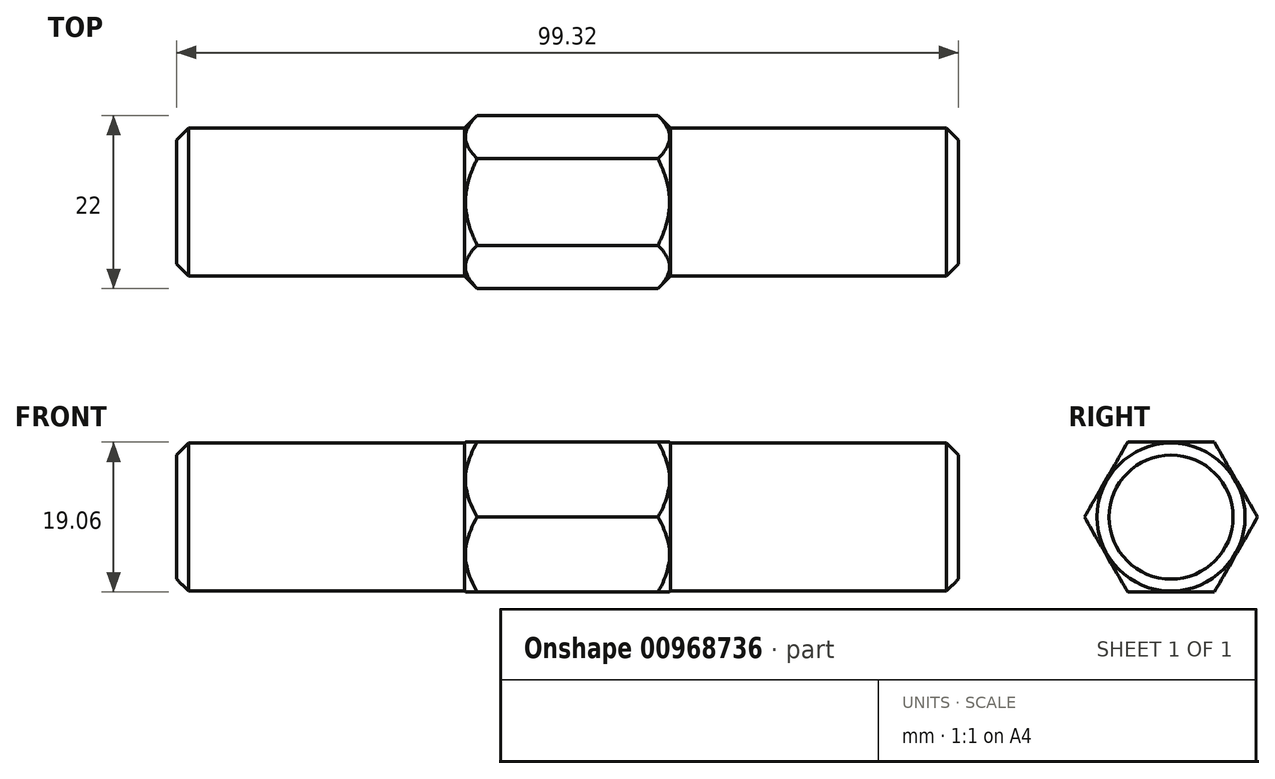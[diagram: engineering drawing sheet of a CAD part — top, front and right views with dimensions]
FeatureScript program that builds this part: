
annotation { "Feature Type Name" : "Feature", "Feature Type Description" : "" }
export const myFeature = defineFeature(function(context is Context, id is Id, definition is map)
    precondition{}
    {
        {
            var Q0;
            Q0=qCreatedBy(makeId("Right.planeOp"),FACE);
            var sketch = newSketch(context, id + "F0", { "sketchPlane" : qUnion([Q0])});
            skCircle(sketch, "E0.cCircle", {"center": v(0, 0) * mm, "radius": 9.53 * mm, "construction": true});
            skLineSegment(sketch, "E0.0", {"start": v(11, 0) * mm, "end": v(5.5, -9.53) * mm});
            skLineSegment(sketch, "E0.1", {"start": v(5.5, -9.53) * mm, "end": v(-5.5, -9.53) * mm});
            skLineSegment(sketch, "E0.2", {"start": v(-5.5, -9.52) * mm, "end": v(-11, 0) * mm});
            skLineSegment(sketch, "E0.3", {"start": v(-11, 0) * mm, "end": v(-5.5, 9.52) * mm});
            skLineSegment(sketch, "E0.4", {"start": v(-5.5, 9.52) * mm, "end": v(5.5, 9.52) * mm});
            skLineSegment(sketch, "E0.5", {"start": v(5.5, 9.52) * mm, "end": v(11, 0) * mm});
            skPoint(sketch, "E0.0.midPoint", {"position": v(8.25, -4.76) * mm});
            skSolve(sketch);
        }
        {
            var Q0;
            Q0=makeQuery(id+"F0.imprint","IMPRINT",FACE,{"disambiguationData":[TD([[makeQuery(id+"F0.imprint","IMPRINT",EDGE,{"derivedFrom":sQuery(id+"F0.wireOp",EDGE,"E0.0")}),-1.0]])]});
            extrude(context, id + "F1", {"entities" : qUnion([Q0]), "depth" : 13.08 * mm, "offsetDistance" : 25.4 * mm});
        }
        {
            var Q0;
            Q0=makeQuery(id+"F1.opExtrude","CAP_FACE",FACE,{"disambiguationData":[OSD([sQuery(id+"F0.wireOp",EDGE,"E0.0"),sQuery(id+"F0.wireOp",EDGE,"E0.1"),sQuery(id+"F0.wireOp",EDGE,"E0.2"),sQuery(id+"F0.wireOp",EDGE,"E0.3"),sQuery(id+"F0.wireOp",EDGE,"E0.4"),sQuery(id+"F0.wireOp",EDGE,"E0.5")])],"isStart":false});
            var sketch = newSketch(context, id + "F2", { "sketchPlane" : qUnion([Q0])});
            skCircle(sketch, "E1", {"center": v(0, 0) * mm, "radius": 9.4 * mm});
            skSolve(sketch);
        }
        {
            var Q0;
            Q0=makeQuery(id+"F2.imprint","IMPRINT",FACE,{"disambiguationData":[TD([[makeQuery(id+"F2.imprint","IMPRINT",EDGE,{"derivedFrom":sQuery(id+"F2.wireOp",EDGE,"E1")}),1.0]])]});
            extrude(context, id + "F3", {"entities" : qUnion([Q0]), "operationType" : NewBodyOperationType.ADD, "depth" : 36.58 * mm, "offsetDistance" : 25.4 * mm});
        }
        {
            var Q0;
            Q0=makeQuery(id+"F3.opExtrude","CAP_EDGE",EDGE,{"disambiguationData":[OSD([sQuery(id+"F2.wireOp",EDGE,"E1")])],"isStart":false});
            chamfer(context, id + "F4", {"entities" : qUnion([Q0]), "width" : 1.52 * mm, "tangentPropagation" : true});
        }
        {
            var Q0;
            Q0=qCreatedBy(makeId("Top.planeOp"),FACE);
            var sketch = newSketch(context, id + "F5", { "sketchPlane" : qUnion([Q0])});
            skLineSegment(sketch, "E2", {"start": v(13.08, 11.43) * mm, "end": v(11.05, 11.43) * mm});
            skLineSegment(sketch, "E3", {"start": v(50.45, 0) * mm, "end": v(-11.13, 0) * mm, "construction": true});
            skLineSegment(sketch, "E4", {"start": v(13.08, 11.43) * mm, "end": v(13.08, 9.4) * mm});
            skLineSegment(sketch, "E5", {"start": v(11.05, 11.43) * mm, "end": v(13.08, 9.4) * mm});
            skSolve(sketch);
        }
        {
            var Q0;
            Q0=makeQuery(id+"F5.imprint","IMPRINT",FACE,{"disambiguationData":[TD([[makeQuery(id+"F5.imprint","IMPRINT",EDGE,{"derivedFrom":sQuery(id+"F5.wireOp",EDGE,"E2")}),1.0]])]});
            var Q1;
            Q1=sQuery(id+"F5.wireOp",EDGE,"E3");
            revolve(context, id + "F6", {"operationType" : NewBodyOperationType.REMOVE, "surfaceOperationType" : NewSurfaceOperationType.NEW, "entities" : qUnion([Q0]), "axis" : qUnion([Q1]), "revolveType" : RevolveType.FULL, "oppositeDirection" : true});
        }
        {
            var Q0;
            Q0=makeQuery(id+"F1.opExtrude","SWEPT_BODY",BODY,{"disambiguationData":[OSD([sQuery(id+"F0.wireOp",EDGE,"E0.0"),sQuery(id+"F0.wireOp",EDGE,"E0.1"),sQuery(id+"F0.wireOp",EDGE,"E0.2"),sQuery(id+"F0.wireOp",EDGE,"E0.3"),sQuery(id+"F0.wireOp",EDGE,"E0.4"),sQuery(id+"F0.wireOp",EDGE,"E0.5")])]});
            var Q1;
            Q1=makeQuery(id+"F1.opExtrude","CAP_FACE",FACE,{"disambiguationData":[OSD([sQuery(id+"F0.wireOp",EDGE,"E0.0"),sQuery(id+"F0.wireOp",EDGE,"E0.1"),sQuery(id+"F0.wireOp",EDGE,"E0.2"),sQuery(id+"F0.wireOp",EDGE,"E0.3"),sQuery(id+"F0.wireOp",EDGE,"E0.4"),sQuery(id+"F0.wireOp",EDGE,"E0.5")])],"isStart":true});
            mirror(context, id + "F7", {"operationType" : NewBodyOperationType.ADD, "entities" : qUnion([Q0]), "mirrorPlane" : qUnion([Q1])});
        }
    });
